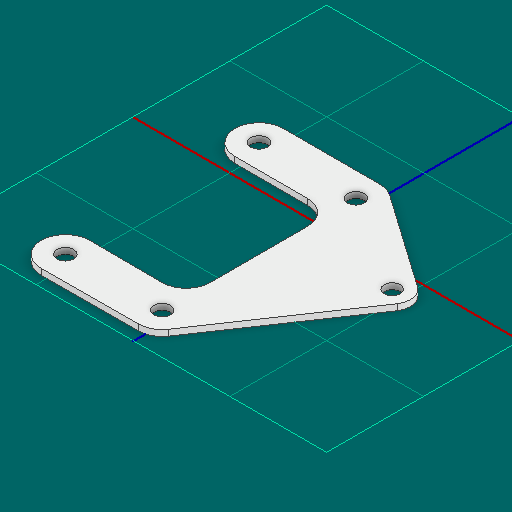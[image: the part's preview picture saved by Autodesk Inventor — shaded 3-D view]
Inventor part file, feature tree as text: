
AUTODESK INVENTOR PART (.ipt)
format: ipt  version: 2025 (Build 290162000, 162)  size: 130,560 bytes
history: native  units: in
note: dims shown in document units (in); Inventor stores cm internally (conversion verified against a paired STEP export)
features: extrude x1, sketch x1
ambient origin geometry x8: Origin, YZ Plane, XZ Plane, XY Plane, X Axis, Y Axis, Z Axis, Center Point
bodies: Solid1 (feature_tree)
feature tree (2):
  extrude  "Extrusion1"  Depth=0.0625in TaperAngle=0.0deg
  sketch  "Sketch1"  dims[d0=0.165in d1=0.375in d2=1.0in d3=0.25in d4=0.0625in d5=0.0in]
